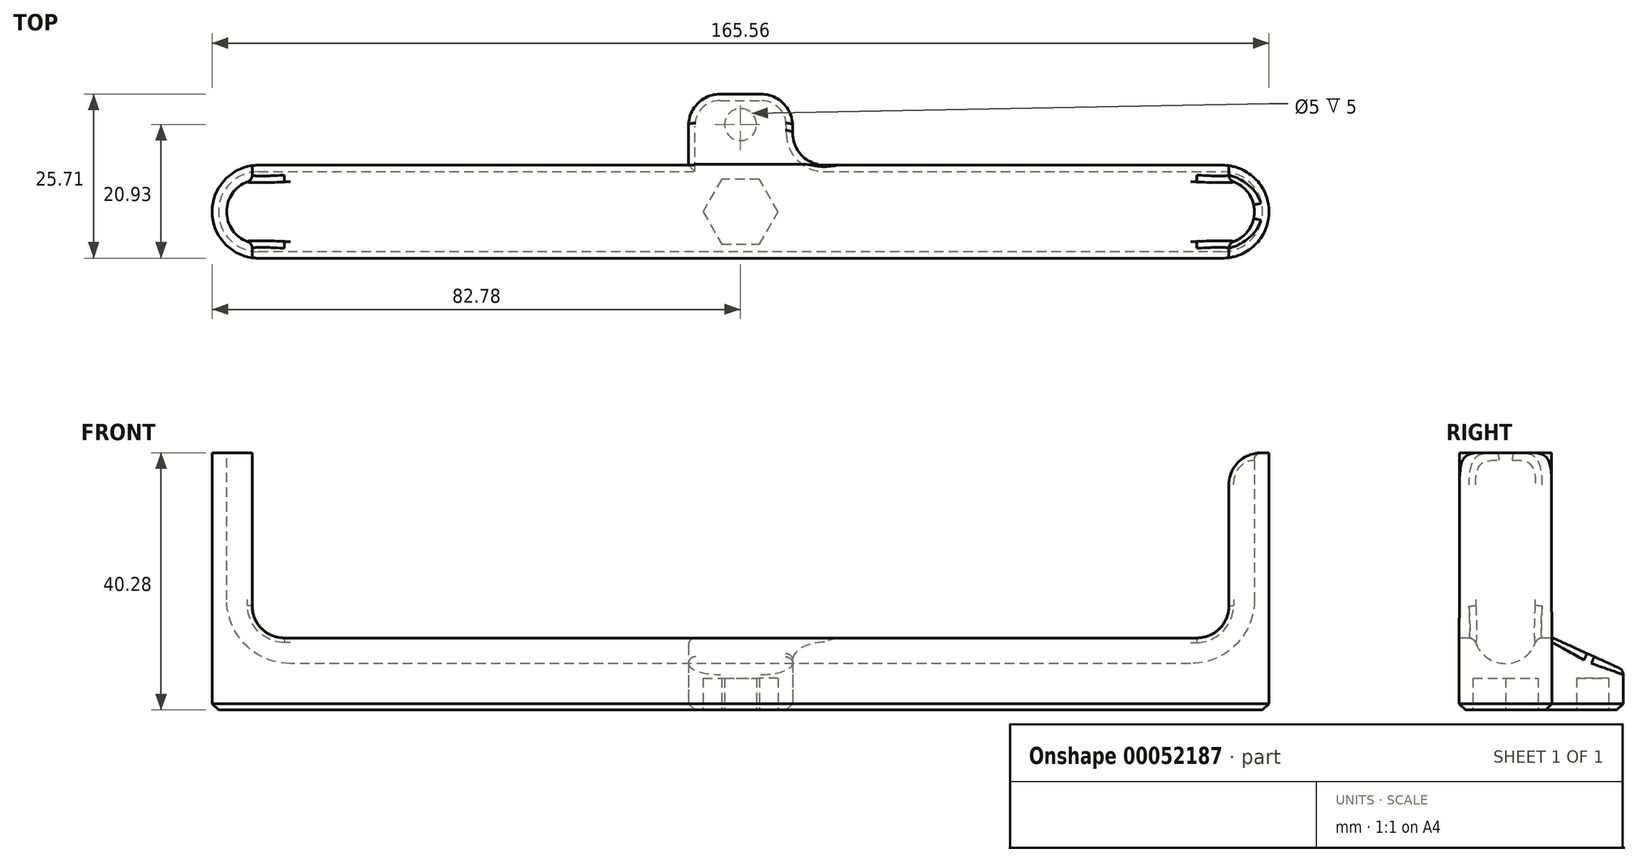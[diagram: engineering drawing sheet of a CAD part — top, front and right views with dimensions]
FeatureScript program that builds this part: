
annotation { "Feature Type Name" : "Feature", "Feature Type Description" : "" }
export const myFeature = defineFeature(function(context is Context, id is Id, definition is map)
    precondition{}
    {
        {
            assignVariable(context, id + "F0", {"name" : "thickness", "anyValue" : 10});
        }
        {
            assignVariable(context, id + "F1", {"name" : "line_width", "anyValue" : 0.48});
        }
        {
            assignVariable(context, id + "F2", {"name" : "side_wall", "anyValue" : 0.95 * (getVariable(context, 'line_width') * 5)});
        }
        {
            assignVariable(context, id + "F3", {"name" : "M6_height", "anyValue" : 5});
        }
        {
            assignVariable(context, id + "F4", {"name" : "sides", "anyValue" : 33 + getVariable(context, 'side_wall') + getVariable(context, 'M6_height')});
        }
        {
            var Q0;
            Q0=qCreatedBy(makeId("Top.planeOp"),FACE);
            var sketch = newSketch(context, id + "F5", { "sketchPlane" : qUnion([Q0])});
            skLineSegment(sketch, "E0.rect.bottom", {"start": v(82.78, -7.28) * mm, "end": v(-82.78, -7.28) * mm});
            skLineSegment(sketch, "E0.rect.top", {"start": v(82.78, 7.28) * mm, "end": v(-82.78, 7.28) * mm});
            skLineSegment(sketch, "E0.rect.left", {"start": v(82.78, -7.28) * mm, "end": v(82.78, 7.28) * mm});
            skLineSegment(sketch, "E0.rect.right", {"start": v(-82.78, -7.28) * mm, "end": v(-82.78, 7.28) * mm});
            skPoint(sketch, "E0.rect.middle", {"position": v(0, 0) * mm});
            skSolve(sketch);
        }
        {
            var Q0;
            Q0=makeQuery(id+"F5.imprint","IMPRINT",FACE,{"disambiguationData":[TD([[makeQuery(id+"F5.imprint","IMPRINT",EDGE,{"derivedFrom":sQuery(id+"F5.wireOp",EDGE,"E0.rect.bottom")}),-1.0]])]});
            extrude(context, id + "F6", {"entities" : qUnion([Q0]), "depth" : (getVariable(context, 'sides')) * mm});
        }
        {
            var Q0;
            Q0=qCreatedBy(makeId("Front.planeOp"),FACE);
            var sketch = newSketch(context, id + "F7", { "sketchPlane" : qUnion([Q0])});
            skLineSegment(sketch, "E1.rect.bottom", {"start": v(70.5, 7.28) * mm, "end": v(-70.5, 7.28) * mm});
            skLineSegment(sketch, "E1.rect.top", {"start": v(70.5, 88.28) * mm, "end": v(-70.5, 88.28) * mm});
            skLineSegment(sketch, "E1.rect.left", {"start": v(80.5, 17.28) * mm, "end": v(80.5, 78.28) * mm});
            skLineSegment(sketch, "E1.rect.right", {"start": v(-80.5, 17.28) * mm, "end": v(-80.5, 78.28) * mm});
            skPoint(sketch, "E1.rect.middle", {"position": v(0, 47.78) * mm});
            skPoint(sketch, "E2.visualSharp", {"position": v(-80.5, 88.28) * mm});
            skArc(sketch, "E2.filletArc", {"start": v(-70.5, 88.28) * mm, "mid": v(-77.57, 85.35) * mm, "end": v(-80.5, 78.28) * mm});
            skPoint(sketch, "E3.visualSharp", {"position": v(80.5, 88.28) * mm});
            skArc(sketch, "E3.filletArc", {"start": v(80.5, 78.28) * mm, "mid": v(77.57, 85.35) * mm, "end": v(70.5, 88.28) * mm});
            skPoint(sketch, "E4.visualSharp", {"position": v(80.5, 7.28) * mm});
            skArc(sketch, "E4.filletArc", {"start": v(70.5, 7.28) * mm, "mid": v(77.57, 10.2) * mm, "end": v(80.5, 17.28) * mm});
            skPoint(sketch, "E5.visualSharp", {"position": v(-80.5, 7.28) * mm});
            skArc(sketch, "E5.filletArc", {"start": v(-80.5, 17.28) * mm, "mid": v(-77.57, 10.2) * mm, "end": v(-70.5, 7.28) * mm});
            skSolve(sketch);
        }
        {
            var Q0;
            Q0 = qSketchRegion(id + "F7", true);
            extrude(context, id + "F8", {"entities" : qUnion([Q0]), "endBound" : BoundingType.SYMMETRIC, "depth" : (getVariable(context, 'thickness')) * mm});
        }
        {
            var Q0;
            Q0=makeQuery(id+"F8.opExtrude","CAP_EDGE",EDGE,{"disambiguationData":[OSD([sQuery(id+"F7.wireOp",EDGE,"E1.rect.top")])],"isStart":false});
            var Q1;
            Q1=makeQuery(id+"F8.opExtrude","CAP_EDGE",EDGE,{"disambiguationData":[OSD([sQuery(id+"F7.wireOp",EDGE,"E1.rect.top")])],"isStart":true});
            fillet(context, id + "F9", {"entities" : qUnion([Q0, Q1]), "radius" : (getVariable(context, 'thickness') / 2) * mm, "tangentPropagation" : true, "allowEdgeOverflow" : false});
        }
        {
            var Q0;
            Q0=makeQuery(id+"F8.opExtrude","SWEPT_BODY",BODY,{"disambiguationData":[OSD([sQuery(id+"F7.wireOp",EDGE,"E1.rect.bottom"),sQuery(id+"F7.wireOp",EDGE,"E1.rect.top"),sQuery(id+"F7.wireOp",EDGE,"E1.rect.left"),sQuery(id+"F7.wireOp",EDGE,"E1.rect.right"),sQuery(id+"F7.wireOp",EDGE,"E2.filletArc"),sQuery(id+"F7.wireOp",EDGE,"E3.filletArc"),sQuery(id+"F7.wireOp",EDGE,"E4.filletArc"),sQuery(id+"F7.wireOp",EDGE,"E5.filletArc")])]});
            var Q1;
            Q1=makeQuery(id+"F6.opExtrude","SWEPT_BODY",BODY,{"disambiguationData":[OSD([sQuery(id+"F5.wireOp",EDGE,"E0.rect.bottom"),sQuery(id+"F5.wireOp",EDGE,"E0.rect.top"),sQuery(id+"F5.wireOp",EDGE,"E0.rect.left"),sQuery(id+"F5.wireOp",EDGE,"E0.rect.right")])]});
            booleanBodies(context, id + "F10", {"operationType" : BooleanOperationType.SUBTRACTION, "tools" : qUnion([Q0]), "targets" : qUnion([Q1])});
        }
        {
            var Q0;
            Q0=makeQuery(id+"F6.opExtrude","SWEPT_FACE",FACE,{"disambiguationData":[OSD([sQuery(id+"F5.wireOp",EDGE,"E0.rect.bottom")])]});
            var sketch = newSketch(context, id + "F11", { "sketchPlane" : qUnion([Q0])});
            skLineSegment(sketch, "E6.rect.bottom", {"start": v(-76.5, 40.28) * mm, "end": v(76.5, 40.28) * mm});
            skLineSegment(sketch, "E6.rect.top", {"start": v(-76.5, 11.28) * mm, "end": v(76.5, 11.28) * mm});
            skLineSegment(sketch, "E6.rect.left", {"start": v(-76.5, 40.28) * mm, "end": v(-76.5, 11.28) * mm});
            skLineSegment(sketch, "E6.rect.right", {"start": v(76.5, 40.28) * mm, "end": v(76.5, 11.28) * mm});
            skPoint(sketch, "E6.rect.middle", {"position": v(0, 25.78) * mm});
            skPoint(sketch, "E6.rect.middle.positionSnap0", {"position": v(0, 40.28) * mm});
            skPoint(sketch, "E6.rect.centerSnap0", {"position": v(0, 40.28) * mm});
            skSolve(sketch);
        }
        {
            var Q0;
            Q0=makeQuery(id+"F11.imprint","IMPRINT",FACE,{"disambiguationData":[TD([[makeQuery(id+"F11.imprint","IMPRINT",EDGE,{"derivedFrom":sQuery(id+"F11.wireOp",EDGE,"E6.rect.bottom")}),1.0]])]});
            var Q1;
            Q1=makeQuery(id+"F6.opExtrude","SWEPT_FACE",FACE,{"disambiguationData":[OSD([sQuery(id+"F5.wireOp",EDGE,"E0.rect.top")])]});
            extrude(context, id + "F12", {"entities" : qUnion([Q0]), "operationType" : NewBodyOperationType.REMOVE, "endBound" : BoundingType.UP_TO_SURFACE, "oppositeDirection" : true, "endBoundEntityFace" : qUnion([Q1]), "depth" : 25 * mm});
        }
        {
            var Q0;
            Q0=makeQuery(id+"F6.opExtrude","SWEPT_EDGE",EDGE,{"disambiguationData":[OSD([sQuery(id+"F5.wireOp",EDGE,"E0.rect.top"),sQuery(id+"F5.wireOp",EDGE,"E0.rect.left")])]});
            var Q1;
            Q1=makeQuery(id+"F6.opExtrude","SWEPT_EDGE",EDGE,{"disambiguationData":[OSD([sQuery(id+"F5.wireOp",EDGE,"E0.rect.bottom"),sQuery(id+"F5.wireOp",EDGE,"E0.rect.left")])]});
            var Q2;
            Q2=makeQuery(id+"F6.opExtrude","SWEPT_EDGE",EDGE,{"disambiguationData":[OSD([sQuery(id+"F5.wireOp",EDGE,"E0.rect.top"),sQuery(id+"F5.wireOp",EDGE,"E0.rect.right")])]});
            var Q3;
            Q3=makeQuery(id+"F6.opExtrude","SWEPT_EDGE",EDGE,{"disambiguationData":[OSD([sQuery(id+"F5.wireOp",EDGE,"E0.rect.bottom"),sQuery(id+"F5.wireOp",EDGE,"E0.rect.right")])]});
            fillet(context, id + "F13", {"entities" : qUnion([Q0, Q1, Q2, Q3]), "radius" : (5 + getVariable(context, 'side_wall')) * mm, "tangentPropagation" : true, "allowEdgeOverflow" : false});
        }
        {
            var Q0;
            {var subQ0=sQuery(id+"F5.wireOp",EDGE,"E0.rect.bottom");var subQ1=sQuery(id+"F5.wireOp",EDGE,"E0.rect.top");var subQ4=sQuery(id+"F11.wireOp",EDGE,"E6.rect.right");var subQ6=makeQuery(id+"F12.opExtrude","SWEPT_EDGE",EDGE,{"disambiguationData":[OSD([subQ0,sQuery(id+"F11.wireOp",EDGE,"E6.rect.bottom"),subQ4])]});Q0=qUnion([makeQuery(id+"F12.boolean.opBoolean","COPY",EDGE,{"disambiguationData":[TD([makeQuery(id+"F6.opExtrude","SWEPT_FACE",FACE,{"disambiguationData":[OSD([subQ1])]})])],"derivedFrom":subQ6}),makeQuery(id+"F12.boolean.opBoolean","COPY",EDGE,{"disambiguationData":[TD([makeQuery(id+"F6.opExtrude","SWEPT_FACE",FACE,{"disambiguationData":[OSD([subQ0])]})])],"derivedFrom":subQ6})]);}
            var Q1;
            {var subQ0=sQuery(id+"F5.wireOp",EDGE,"E0.rect.bottom");var subQ1=sQuery(id+"F5.wireOp",EDGE,"E0.rect.top");var subQ4=sQuery(id+"F11.wireOp",EDGE,"E6.rect.left");var subQ6=makeQuery(id+"F12.opExtrude","SWEPT_EDGE",EDGE,{"disambiguationData":[OSD([subQ0,sQuery(id+"F11.wireOp",EDGE,"E6.rect.bottom"),subQ4])]});Q1=qUnion([makeQuery(id+"F12.boolean.opBoolean","COPY",EDGE,{"disambiguationData":[TD([makeQuery(id+"F6.opExtrude","SWEPT_FACE",FACE,{"disambiguationData":[OSD([subQ1])]})])],"derivedFrom":subQ6}),makeQuery(id+"F12.boolean.opBoolean","COPY",EDGE,{"disambiguationData":[TD([makeQuery(id+"F6.opExtrude","SWEPT_FACE",FACE,{"disambiguationData":[OSD([subQ0])]})])],"derivedFrom":subQ6})]);}
            var Q2;
            {var subQ1=sQuery(id+"F11.wireOp",EDGE,"E6.rect.top");var subQ3=sQuery(id+"F11.wireOp",EDGE,"E6.rect.left");var subQ5=makeQuery(id+"F12.opExtrude","SWEPT_EDGE",EDGE,{"disambiguationData":[OSD([subQ1,subQ3])]});Q2=qUnion([makeQuery(id+"F12.boolean.opBoolean","COPY",EDGE,{"disambiguationData":[TD([makeQuery(id+"F6.opExtrude","SWEPT_FACE",FACE,{"disambiguationData":[OSD([sQuery(id+"F5.wireOp",EDGE,"E0.rect.top")])]})])],"derivedFrom":subQ5}),makeQuery(id+"F12.boolean.opBoolean","COPY",EDGE,{"disambiguationData":[TD([makeQuery(id+"F6.opExtrude","SWEPT_FACE",FACE,{"disambiguationData":[OSD([sQuery(id+"F5.wireOp",EDGE,"E0.rect.bottom")])]})])],"derivedFrom":subQ5})]);}
            var Q3;
            {var subQ1=sQuery(id+"F11.wireOp",EDGE,"E6.rect.top");var subQ3=sQuery(id+"F11.wireOp",EDGE,"E6.rect.left");var subQ5=makeQuery(id+"F12.opExtrude","SWEPT_EDGE",EDGE,{"disambiguationData":[OSD([subQ1,subQ3])]});Q3=qUnion([makeQuery(id+"F12.boolean.opBoolean","COPY",EDGE,{"disambiguationData":[TD([makeQuery(id+"F6.opExtrude","SWEPT_FACE",FACE,{"disambiguationData":[OSD([sQuery(id+"F5.wireOp",EDGE,"E0.rect.top")])]})])],"derivedFrom":subQ5}),makeQuery(id+"F12.boolean.opBoolean","COPY",EDGE,{"disambiguationData":[TD([makeQuery(id+"F6.opExtrude","SWEPT_FACE",FACE,{"disambiguationData":[OSD([sQuery(id+"F5.wireOp",EDGE,"E0.rect.bottom")])]})])],"derivedFrom":subQ5})]);}
            var Q4;
            {var subQ1=sQuery(id+"F11.wireOp",EDGE,"E6.rect.right");var subQ3=sQuery(id+"F11.wireOp",EDGE,"E6.rect.top");var subQ5=makeQuery(id+"F12.opExtrude","SWEPT_EDGE",EDGE,{"disambiguationData":[OSD([subQ3,subQ1])]});Q4=qUnion([makeQuery(id+"F12.boolean.opBoolean","COPY",EDGE,{"disambiguationData":[TD([makeQuery(id+"F6.opExtrude","SWEPT_FACE",FACE,{"disambiguationData":[OSD([sQuery(id+"F5.wireOp",EDGE,"E0.rect.top")])]})])],"derivedFrom":subQ5}),makeQuery(id+"F12.boolean.opBoolean","COPY",EDGE,{"disambiguationData":[TD([makeQuery(id+"F6.opExtrude","SWEPT_FACE",FACE,{"disambiguationData":[OSD([sQuery(id+"F5.wireOp",EDGE,"E0.rect.bottom")])]})])],"derivedFrom":subQ5})]);}
            var Q5;
            {var subQ1=sQuery(id+"F11.wireOp",EDGE,"E6.rect.right");var subQ3=sQuery(id+"F11.wireOp",EDGE,"E6.rect.top");var subQ5=makeQuery(id+"F12.opExtrude","SWEPT_EDGE",EDGE,{"disambiguationData":[OSD([subQ3,subQ1])]});Q5=qUnion([makeQuery(id+"F12.boolean.opBoolean","COPY",EDGE,{"disambiguationData":[TD([makeQuery(id+"F6.opExtrude","SWEPT_FACE",FACE,{"disambiguationData":[OSD([sQuery(id+"F5.wireOp",EDGE,"E0.rect.top")])]})])],"derivedFrom":subQ5}),makeQuery(id+"F12.boolean.opBoolean","COPY",EDGE,{"disambiguationData":[TD([makeQuery(id+"F6.opExtrude","SWEPT_FACE",FACE,{"disambiguationData":[OSD([sQuery(id+"F5.wireOp",EDGE,"E0.rect.bottom")])]})])],"derivedFrom":subQ5})]);}
            fillet(context, id + "F14", {"entities" : qUnion([Q0, Q1, Q2, Q3, Q4, Q5]), "radius" : 5 * mm, "tangentPropagation" : true, "allowEdgeOverflow" : false});
        }
        {
            var Q0;
            Q0=makeQuery(id+"F6.opExtrude","CAP_FACE",FACE,{"disambiguationData":[OSD([sQuery(id+"F5.wireOp",EDGE,"E0.rect.bottom"),sQuery(id+"F5.wireOp",EDGE,"E0.rect.top"),sQuery(id+"F5.wireOp",EDGE,"E0.rect.left"),sQuery(id+"F5.wireOp",EDGE,"E0.rect.right")])],"isStart":true});
            var sketch = newSketch(context, id + "F15", { "sketchPlane" : qUnion([Q0])});
            skLineSegment(sketch, "E7.bottom", {"start": v(-8.17, 7.28) * mm, "end": v(8.17, 7.28) * mm});
            skLineSegment(sketch, "E7.top", {"start": v(-3.17, -18.43) * mm, "end": v(3.17, -18.43) * mm});
            skLineSegment(sketch, "E7.left", {"start": v(-8.17, 7.28) * mm, "end": v(-8.17, -13.43) * mm});
            skLineSegment(sketch, "E7.right", {"start": v(8.17, 7.28) * mm, "end": v(8.17, -13.43) * mm});
            skCircle(sketch, "E8.cCircle", {"center": v(0, 0) * mm, "radius": 5.1 * mm, "construction": true});
            skLineSegment(sketch, "E8.0", {"start": v(5.89, 0) * mm, "end": v(2.94, -5.1) * mm});
            skLineSegment(sketch, "E8.1", {"start": v(2.94, -5.1) * mm, "end": v(-2.94, -5.1) * mm});
            skLineSegment(sketch, "E8.2", {"start": v(-2.94, -5.1) * mm, "end": v(-5.89, 0) * mm});
            skLineSegment(sketch, "E8.3", {"start": v(-5.89, 0) * mm, "end": v(-2.94, 5.1) * mm});
            skLineSegment(sketch, "E8.4", {"start": v(-2.94, 5.1) * mm, "end": v(2.94, 5.1) * mm});
            skLineSegment(sketch, "E8.5", {"start": v(2.94, 5.1) * mm, "end": v(5.89, 0) * mm});
            skPoint(sketch, "E8.0.midPoint", {"position": v(4.42, -2.55) * mm});
            skLineSegment(sketch, "E9", {"start": v(5.89, 0) * mm, "end": v(8.17, 0) * mm, "construction": true});
            skLineSegment(sketch, "E10", {"start": v(-5.89, 0) * mm, "end": v(-8.17, 0) * mm, "construction": true});
            skCircle(sketch, "E11", {"center": v(0, -13.65) * mm, "radius": 2.5 * mm});
            skPoint(sketch, "E12.visualSharp", {"position": v(-8.17, -18.43) * mm});
            skArc(sketch, "E12.filletArc", {"start": v(-8.17, -13.43) * mm, "mid": v(-6.7, -16.97) * mm, "end": v(-3.17, -18.43) * mm});
            skPoint(sketch, "E13.visualSharp", {"position": v(8.17, -18.43) * mm});
            skArc(sketch, "E13.filletArc", {"start": v(3.17, -18.43) * mm, "mid": v(6.7, -16.97) * mm, "end": v(8.17, -13.43) * mm});
            skSolve(sketch);
        }
        {
            var Q0;
            Q0=makeQuery(id+"F15.imprint","IMPRINT",FACE,{"disambiguationData":[TD([[makeQuery(id+"F15.imprint","IMPRINT",EDGE,{"derivedFrom":sQuery(id+"F15.wireOp",EDGE,"E7.top")}),1.0]])]});
            var Q1;
            Q1=makeQuery(id+"F15.imprint","IMPRINT",FACE,{"disambiguationData":[TD([[makeQuery(id+"F15.imprint","IMPRINT",EDGE,{"derivedFrom":sQuery(id+"F15.wireOp",EDGE,"E11")}),1.0]])]});
            var Q2;
            {var subQ5=makeQuery(id+"F12.opExtrude","SWEPT_FACE",FACE,{"disambiguationData":[OSD([sQuery(id+"F11.wireOp",EDGE,"E6.rect.top")])]});Q2=qUnion([makeQuery(id+"F12.boolean.opBoolean","COPY",FACE,{"disambiguationData":[TD([makeQuery(id+"F6.opExtrude","SWEPT_FACE",FACE,{"disambiguationData":[OSD([sQuery(id+"F5.wireOp",EDGE,"E0.rect.top")])]})])],"derivedFrom":subQ5}),makeQuery(id+"F12.boolean.opBoolean","COPY",FACE,{"disambiguationData":[TD([makeQuery(id+"F6.opExtrude","SWEPT_FACE",FACE,{"disambiguationData":[OSD([sQuery(id+"F5.wireOp",EDGE,"E0.rect.bottom")])]})])],"derivedFrom":subQ5})]);}
            extrude(context, id + "F16", {"entities" : qUnion([Q0, Q1]), "operationType" : NewBodyOperationType.ADD, "endBound" : BoundingType.UP_TO_SURFACE, "oppositeDirection" : true, "endBoundEntityFace" : qUnion([Q2]), "depth" : 25 * mm});
        }
        {
            var Q0;
            Q0=makeQuery(id+"F15.imprint","IMPRINT",FACE,{"disambiguationData":[TD([[makeQuery(id+"F15.imprint","IMPRINT",EDGE,{"derivedFrom":sQuery(id+"F15.wireOp",EDGE,"E11")}),1.0]])]});
            var Q1;
            Q1=makeQuery(id+"F15.imprint","IMPRINT",FACE,{"disambiguationData":[TD([[makeQuery(id+"F15.imprint","IMPRINT",EDGE,{"derivedFrom":sQuery(id+"F15.wireOp",EDGE,"E8.0")}),-1.0]])]});
            extrude(context, id + "F17", {"entities" : qUnion([Q0, Q1]), "operationType" : NewBodyOperationType.REMOVE, "oppositeDirection" : true, "depth" : (getVariable(context, 'M6_height')) * mm});
        }
        {
            var Q0;
            Q0=makeQuery(id+"F16.opExtrude","SWEPT_EDGE",EDGE,{"disambiguationData":[OSD([sQuery(id+"F5.wireOp",EDGE,"E0.rect.top"),sQuery(id+"F15.wireOp",EDGE,"E7.left")])]});
            var Q1;
            Q1=makeQuery(id+"F16.opExtrude","SWEPT_EDGE",EDGE,{"disambiguationData":[OSD([sQuery(id+"F5.wireOp",EDGE,"E0.rect.top"),sQuery(id+"F15.wireOp",EDGE,"E7.right")])]});
            fillet(context, id + "F18", {"entities" : qUnion([Q0, Q1]), "radius" : 5 * mm, "allowEdgeOverflow" : false});
        }
        {
            var Q0;
            Q0=makeQuery(id+"F16.opExtrude","CAP_EDGE",EDGE,{"disambiguationData":[OSD([sQuery(id+"F15.wireOp",EDGE,"E7.top")])],"isStart":false});
            chamfer(context, id + "F19", {"entities" : qUnion([Q0]), "chamferType" : ChamferType.TWO_OFFSETS, "width1" : 11 * mm, "oppositeDirection" : false, "width2" : 5 * mm});
        }
        {
            var Q0;
            {var subQ0=sQuery(id+"F15.wireOp",EDGE,"E7.left");var subQ1=sQuery(id+"F5.wireOp",EDGE,"E0.rect.top");Q0=makeQuery(id+"F16.boolean.opBoolean","SPLIT",EDGE,{"disambiguationData":[TD([makeQuery(id+"F16.opExtrude","SWEPT_FACE",FACE,{"disambiguationData":[OSD([subQ0])]})])],"derivedFrom":makeQuery(id+"F6.opExtrude","CAP_EDGE",EDGE,{"disambiguationData":[OSD([subQ1])],"isStart":true})});}
            chamfer(context, id + "F20", {"entities" : qUnion([Q0]), "width" : 1 * mm, "tangentPropagation" : true});
        }
        {
            var Q0;
            {var subQ0=sQuery(id+"F15.wireOp",EDGE,"E7.left");var subQ4=sQuery(id+"F11.wireOp",EDGE,"E6.rect.top");Q0=makeQuery(id+"F16.boolean.opBoolean","SPLIT",EDGE,{"disambiguationData":[TD([makeQuery(id+"F16.opExtrude","SWEPT_FACE",FACE,{"disambiguationData":[OSD([subQ0])]})])],"derivedFrom":makeQuery(id+"F12.boolean.opBoolean","COPY",EDGE,{"derivedFrom":makeQuery(id+"F12.opExtrude","CAP_EDGE",EDGE,{"disambiguationData":[OSD([subQ4])],"isStart":false})})});}
            var Q1;
            Q1=makeQuery(id+"F12.boolean.opBoolean","INTERSECT",EDGE,{"disambiguationData":[OD(0.0)],"derivedFrom":[makeQuery(id+"F10.opBoolean","COPY",FACE,{"derivedFrom":makeQuery(id+"F9.opFillet","BLEND_FACE",FACE,{"disambiguationData":[OSD([sQuery(id+"F7.wireOp",EDGE,"E1.rect.bottom")])]})}),makeQuery(id+"F12.opExtrude","SWEPT_FACE",FACE,{"disambiguationData":[OSD([sQuery(id+"F11.wireOp",EDGE,"E6.rect.top")])]})]});
            var Q2;
            {var subQ0=sQuery(id+"F15.wireOp",EDGE,"E7.top");Q2=makeQuery(id+"F19.opChamfer","BLEND_EDGE",EDGE,{"blendedFrom":[makeQuery(id+"F16.opExtrude","CAP_EDGE",EDGE,{"disambiguationData":[OSD([subQ0])],"isStart":false}),makeQuery(id+"F16.opExtrude","SWEPT_FACE",FACE,{"disambiguationData":[OSD([subQ0])]})],"blendedInto":[makeQuery(id+"F16.opExtrude","SWEPT_FACE",FACE,{"disambiguationData":[OSD([subQ0])]})]});}
            fillet(context, id + "F21", {"entities" : qUnion([Q0, Q1, Q2]), "radius" : (getVariable(context, 'side_wall') / 2) * mm, "tangentPropagation" : true, "allowEdgeOverflow" : false});
        }
    });
